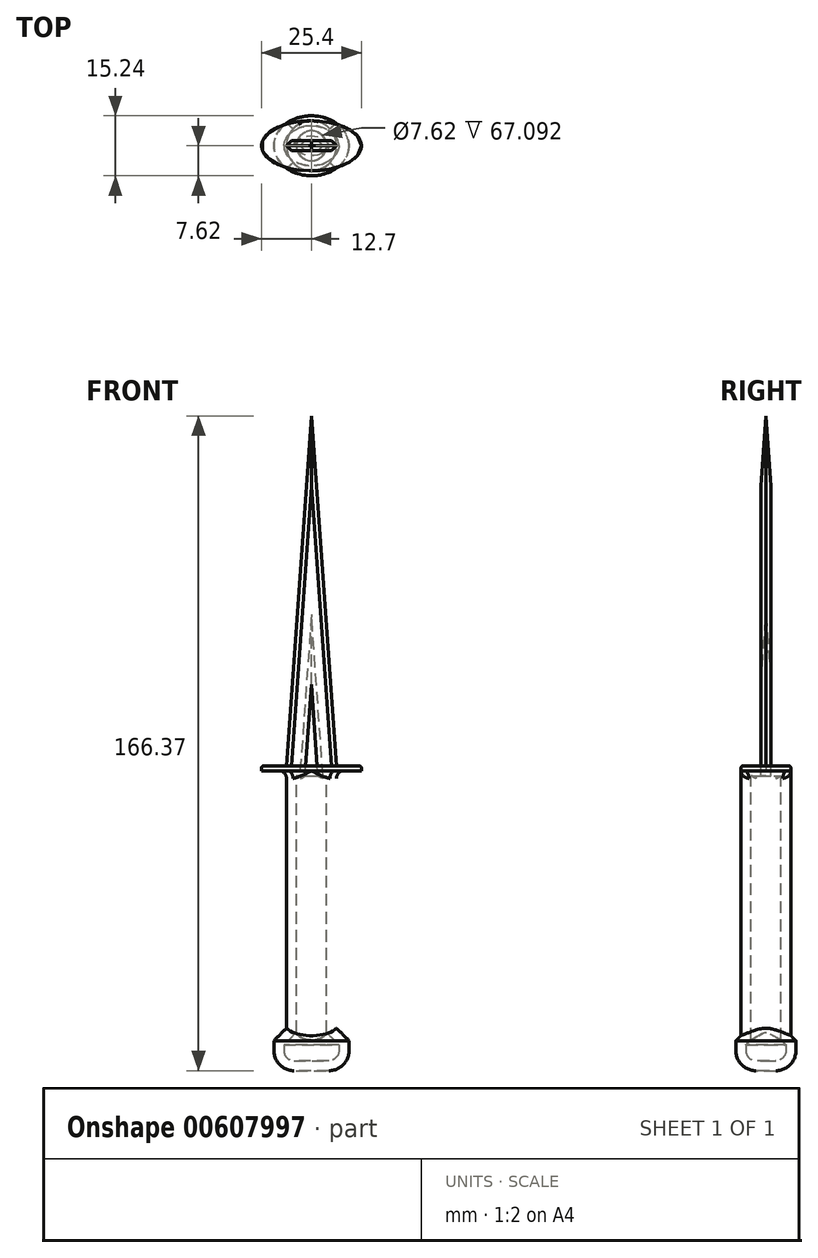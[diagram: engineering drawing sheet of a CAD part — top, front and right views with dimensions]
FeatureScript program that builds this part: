
annotation { "Feature Type Name" : "Feature", "Feature Type Description" : "" }
export const myFeature = defineFeature(function(context is Context, id is Id, definition is map)
    precondition{}
    {
        {
            var Q0;
            Q0=qCreatedBy(makeId("Front.planeOp"),FACE);
            var sketch = newSketch(context, id + "F0", { "sketchPlane" : qUnion([Q0])});
            skPoint(sketch, "E0", {"position": v(-6.35, 0) * mm});
            skPoint(sketch, "E1", {"position": v(6.35, 0) * mm});
            skPoint(sketch, "E2", {"position": v(0, 88.9) * mm});
            skLineSegment(sketch, "E3", {"start": v(-6.35, 0) * mm, "end": v(0, 88.9) * mm});
            skLineSegment(sketch, "E4", {"start": v(6.35, 0) * mm, "end": v(0, 88.9) * mm});
            skLineSegment(sketch, "E5", {"start": v(-6.35, 0) * mm, "end": v(6.35, 0) * mm});
            skSolve(sketch);
        }
        {
            var Q0;
            Q0 = qSketchRegion(id + "F0", true);
            extrude(context, id + "F1", {"entities" : qUnion([Q0]), "depth" : 1.27 * mm, "offsetDistance" : 25.4 * mm});
        }
        {
            var Q0;
            Q0=makeQuery(id+"F1.opExtrude","CAP_FACE",FACE,{"disambiguationData":[OSD([sQuery(id+"F0.wireOp",EDGE,"E3"),sQuery(id+"F0.wireOp",EDGE,"E4"),sQuery(id+"F0.wireOp",EDGE,"E5")])],"isStart":true});
            extrude(context, id + "F2", {"entities" : qUnion([Q0]), "operationType" : NewBodyOperationType.ADD, "depth" : 1.27 * mm, "offsetDistance" : 25.4 * mm});
        }
        {
            var Q0;
            Q0=makeQuery(id+"F2.opExtrude","CAP_EDGE",EDGE,{"disambiguationData":[OSD([sQuery(id+"F0.wireOp",EDGE,"E4")])],"isStart":false});
            var Q1;
            Q1=makeQuery(id+"F2.opExtrude","CAP_EDGE",EDGE,{"disambiguationData":[OSD([sQuery(id+"F0.wireOp",EDGE,"E3")])],"isStart":false});
            var Q2;
            Q2=makeQuery(id+"F1.opExtrude","CAP_EDGE",EDGE,{"disambiguationData":[OSD([sQuery(id+"F0.wireOp",EDGE,"E4")])],"isStart":false});
            var Q3;
            Q3=makeQuery(id+"F1.opExtrude","CAP_EDGE",EDGE,{"disambiguationData":[OSD([sQuery(id+"F0.wireOp",EDGE,"E3")])],"isStart":false});
            chamfer(context, id + "F3", {"entities" : qUnion([Q0, Q1, Q2, Q3]), "width" : 1.27 * mm, "tangentPropagation" : true});
        }
        {
            var Q0;
            Q0=qCreatedBy(makeId("Top.planeOp"),FACE);
            var sketch = newSketch(context, id + "F4", { "sketchPlane" : qUnion([Q0])});
            skEllipse(sketch, "E6", {"center": v(0, 0) * mm, "majorRadius": 12.7 * mm, "minorRadius": 6.35 * mm, "majorAxis": v(1, 0)});
            skSolve(sketch);
        }
        {
            var Q0;
            Q0=makeQuery(id+"F4.imprint","IMPRINT",FACE,{"disambiguationData":[TD([[makeQuery(id+"F4.imprint","IMPRINT",EDGE,{"derivedFrom":sQuery(id+"F4.wireOp",EDGE,"CZl2YhQ6-whO2-7dPJ-9TJx-6SIAmXBnRpKz")}),1.0]])]});
            var Q1;
            {var subQ0=sQuery(id+"F4.wireOp",EDGE,"DZn0rzQc-nCnQ-qjTm-TyfK-i654lKF4WHMA");var subQ1=sQuery(id+"F4.wireOp",EDGE,"CZl2YhQ6-whO2-7dPJ-9TJx-6SIAmXBnRpKz");var subQ2=makeQuery(id+"F4.imprint","INTERSECT",VERTEX,{"disambiguationData":[OD(1.0)],"derivedFrom":[subQ1,subQ0]});Q1=makeQuery(id+"F4.imprint","IMPRINT",FACE,{"disambiguationData":[TD([[makeQuery(id+"F4.imprint","IMPRINT",EDGE,{"disambiguationData":[TD([[subQ2,1.0]])],"derivedFrom":subQ1}),1.0]])]});}
            var Q2;
            {var subQ0=sQuery(id+"F4.wireOp",EDGE,"DZn0rzQc-nCnQ-qjTm-TyfK-i654lKF4WHMA");var subQ1=sQuery(id+"F4.wireOp",EDGE,"CZl2YhQ6-whO2-7dPJ-9TJx-6SIAmXBnRpKz");var subQ2=makeQuery(id+"F4.imprint","INTERSECT",VERTEX,{"disambiguationData":[OD(0.0)],"derivedFrom":[subQ1,subQ0]});Q2=makeQuery(id+"F4.imprint","IMPRINT",FACE,{"disambiguationData":[TD([[makeQuery(id+"F4.imprint","IMPRINT",EDGE,{"disambiguationData":[TD([[subQ2,-1.0]])],"derivedFrom":subQ1}),1.0]])]});}
            var Q3;
            {var subQ0=sQuery(id+"F4.wireOp",EDGE,"507634d2-ae43-4cb0-921a-9d2500652007.trimOffspring");Q3=makeQuery(id+"F4.imprint","IMPRINT",FACE,{"disambiguationData":[TD([[makeQuery(id+"F4.imprint","IMPRINT",EDGE,{"derivedFrom":subQ0}),-1.0]])]});}
            var Q4;
            Q4=makeQuery(id+"F4.imprint","IMPRINT",FACE,{"disambiguationData":[TD([[makeQuery(id+"F4.imprint","IMPRINT",EDGE,{"derivedFrom":sQuery(id+"F4.wireOp",EDGE,"E6")}),1.0]])]});
            extrude(context, id + "F5", {"entities" : qUnion([Q0, Q1, Q2, Q3, Q4]), "operationType" : NewBodyOperationType.ADD, "oppositeDirection" : true, "depth" : 1.27 * mm, "offsetDistance" : 25.4 * mm});
        }
        {
            var Q0;
            Q0=makeQuery(id+"F5.opExtrude","CAP_FACE",FACE,{"disambiguationData":[OSD([sQuery(id+"F4.wireOp",EDGE,"E6")])],"isStart":false});
            var sketch = newSketch(context, id + "F6", { "sketchPlane" : qUnion([Q0])});
            skCircle(sketch, "E7", {"center": v(0, 0) * mm, "radius": 6.35 * mm});
            skSolve(sketch);
        }
        {
            var Q0;
            Q0 = qSketchRegion(id + "F6", true);
            extrude(context, id + "F7", {"entities" : qUnion([Q0]), "operationType" : NewBodyOperationType.ADD, "depth" : 63.5 * mm, "offsetDistance" : 25.4 * mm});
        }
        {
            var Q0;
            {var subQ0=sQuery(id+"F6.wireOp",EDGE,"E7");Q0=makeQuery(id+"F7.boolean.opBoolean","SPLIT",EDGE,{"disambiguationData":[topologyDisambiguationEdgeConnected([makeQuery(id+"F7.opExtrude","SWEPT_FACE",FACE,{"disambiguationData":[OSD([subQ0])]}),makeQuery(id+"F7.opExtrude","CAP_FACE",FACE,{"disambiguationData":[OSD([subQ0])],"isStart":true})]),OD(0.0)],"derivedFrom":makeQuery(id+"F7.opExtrude","CAP_EDGE",EDGE,{"disambiguationData":[OSD([subQ0])],"isStart":true})});}
            var Q1;
            {var subQ0=sQuery(id+"F6.wireOp",EDGE,"E7");Q1=makeQuery(id+"F7.boolean.opBoolean","SPLIT",EDGE,{"disambiguationData":[topologyDisambiguationEdgeConnected([makeQuery(id+"F7.opExtrude","SWEPT_FACE",FACE,{"disambiguationData":[OSD([subQ0])]}),makeQuery(id+"F7.opExtrude","CAP_FACE",FACE,{"disambiguationData":[OSD([subQ0])],"isStart":true})]),OD(1.0)],"derivedFrom":makeQuery(id+"F7.opExtrude","CAP_EDGE",EDGE,{"disambiguationData":[OSD([subQ0])],"isStart":true})});}
            fillet(context, id + "F8", {"entities" : qUnion([Q0, Q1]), "radius" : 1.9 * mm, "tangentPropagation" : true, "allowEdgeOverflow" : false});
        }
        {
            var Q0;
            Q0=makeQuery(id+"F7.opExtrude","CAP_FACE",FACE,{"disambiguationData":[OSD([sQuery(id+"F6.wireOp",EDGE,"E7")])],"isStart":false});
            var sketch = newSketch(context, id + "F9", { "sketchPlane" : qUnion([Q0])});
            skEllipse(sketch, "E8", {"center": v(0, 0) * mm, "majorRadius": 9.53 * mm, "minorRadius": 7.62 * mm, "majorAxis": v(1, 0)});
            skSolve(sketch);
        }
        {
            var Q0;
            Q0 = qSketchRegion(id + "F9", true);
            extrude(context, id + "F10", {"entities" : qUnion([Q0]), "operationType" : NewBodyOperationType.ADD, "depth" : 12.7 * mm, "offsetDistance" : 25.4 * mm});
        }
        {
            var Q0;
            Q0=makeQuery(id+"F10.opExtrude","CAP_EDGE",EDGE,{"disambiguationData":[OSD([sQuery(id+"F9.wireOp",EDGE,"E8")])],"isStart":false});
            fillet(context, id + "F11", {"entities" : qUnion([Q0]), "radius" : 5.08 * mm, "tangentPropagation" : true, "allowEdgeOverflow" : false});
        }
        {
            var Q0;
            Q0=makeQuery(id+"F10.opExtrude","CAP_EDGE",EDGE,{"disambiguationData":[OSD([sQuery(id+"F9.wireOp",EDGE,"E8")])],"isStart":true});
            chamfer(context, id + "F12", {"entities" : qUnion([Q0]), "width" : 5.08 * mm, "tangentPropagation" : true});
        }
        {
            var Q0;
            Q0=makeQuery(id+"F5.opExtrude","CAP_EDGE",EDGE,{"disambiguationData":[OSD([sQuery(id+"F4.wireOp",EDGE,"E6")])],"isStart":true});
            fillet(context, id + "F13", {"entities" : qUnion([Q0]), "radius" : 0.64 * mm, "tangentPropagation" : true, "allowEdgeOverflow" : false});
        }
        {
            var Q0;
            Q0=makeQuery(id+"F1.opExtrude","CAP_FACE",FACE,{"disambiguationData":[OSD([sQuery(id+"F0.wireOp",EDGE,"E3"),sQuery(id+"F0.wireOp",EDGE,"E4"),sQuery(id+"F0.wireOp",EDGE,"E5")])],"isStart":false});
            var Q1;
            Q1=makeQuery(id+"F2.opExtrude","CAP_FACE",FACE,{"disambiguationData":[OSD([sQuery(id+"F0.wireOp",EDGE,"E3"),sQuery(id+"F0.wireOp",EDGE,"E4"),sQuery(id+"F0.wireOp",EDGE,"E5")])],"isStart":false});
            shell(context, id + "F14", {"entities" : qUnion([Q0, Q1]), "thickness" : 2.54 * mm});
        }
    });
